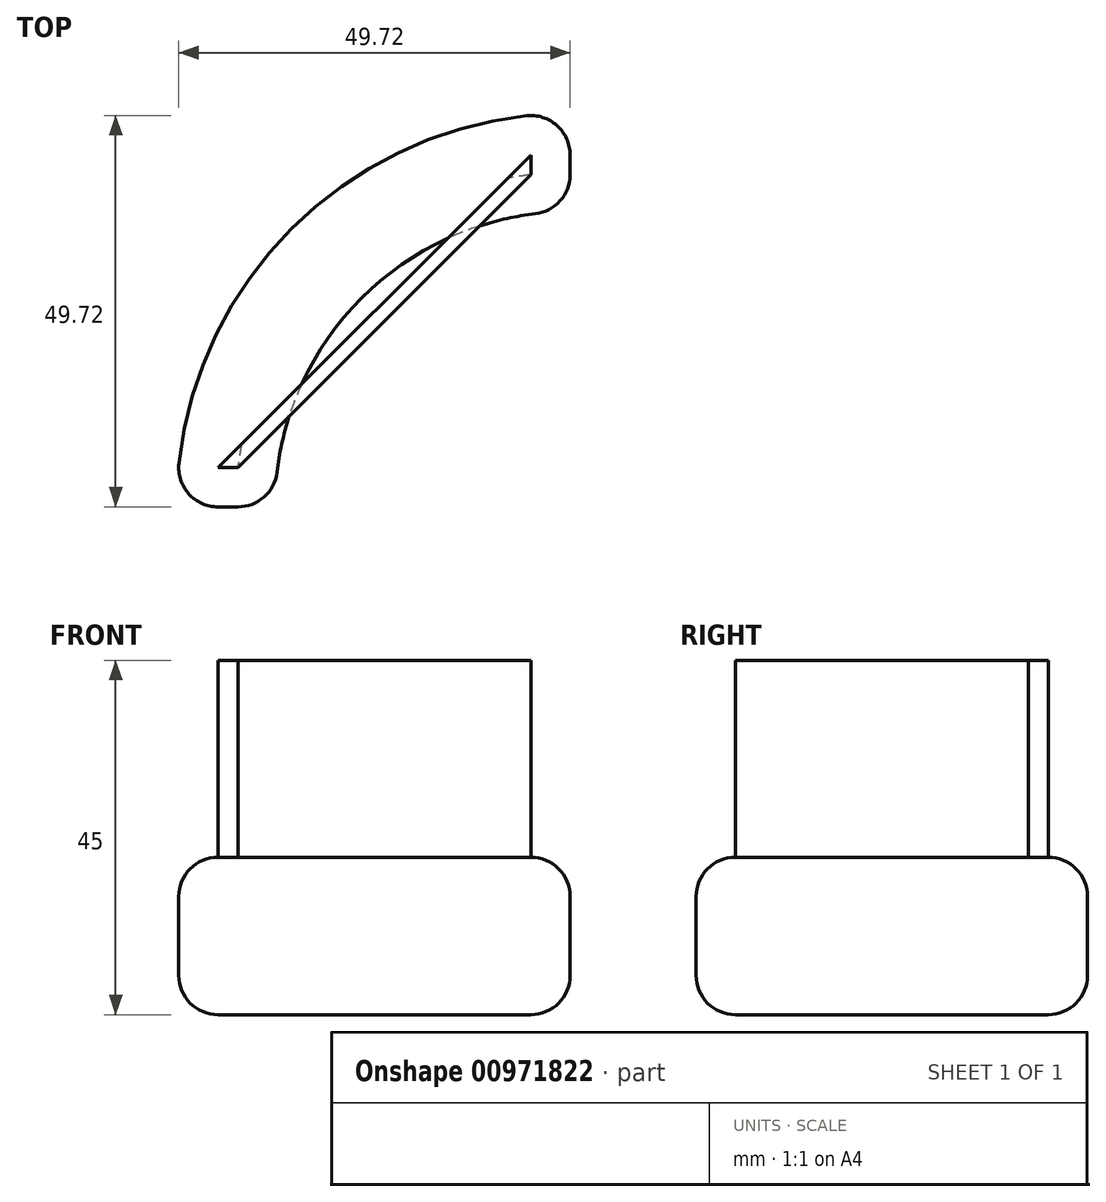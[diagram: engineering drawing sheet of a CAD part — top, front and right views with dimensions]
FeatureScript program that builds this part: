
annotation { "Feature Type Name" : "Feature", "Feature Type Description" : "" }
export const myFeature = defineFeature(function(context is Context, id is Id, definition is map)
    precondition{}
    {
        {
            var Q0;
            Q0=qCreatedBy(makeId("Top.planeOp"),FACE);
            var sketch = newSketch(context, id + "F0", { "sketchPlane" : qUnion([Q0])});
            skArc(sketch, "E0", {"start": v(0, 50) * mm, "mid": v(-35.36, 35.36) * mm, "end": v(-50, 0) * mm});
            skArc(sketch, "E1", {"start": v(0, 37.5) * mm, "mid": v(-26.52, 26.52) * mm, "end": v(-37.5, 0) * mm});
            skLineSegment(sketch, "E2", {"start": v(0, 37.5) * mm, "end": v(0, 50) * mm});
            skLineSegment(sketch, "E3", {"start": v(-37.5, 0) * mm, "end": v(-50, 0) * mm});
            skPoint(sketch, "E4", {"position": v(-37.5, 0) * mm});
            skPoint(sketch, "E5", {"position": v(0, 37.5) * mm});
            skSolve(sketch);
        }
        {
            var Q0;
            Q0 = qSketchRegion(id + "F0", true);
            extrude(context, id + "F1", {"entities" : qUnion([Q0]), "depth" : 20 * mm, "offsetDistance" : 25 * mm});
        }
        {
            var Q0;
            Q0=makeQuery(id+"F1.opExtrude","CAP_EDGE",EDGE,{"disambiguationData":[OSD([sQuery(id+"F0.wireOp",EDGE,"E1")])],"isStart":true});
            var Q1;
            Q1=makeQuery(id+"F1.opExtrude","CAP_EDGE",EDGE,{"disambiguationData":[OSD([sQuery(id+"F0.wireOp",EDGE,"E1")])],"isStart":false});
            var Q2;
            Q2=makeQuery(id+"F1.opExtrude","CAP_EDGE",EDGE,{"disambiguationData":[OSD([sQuery(id+"F0.wireOp",EDGE,"E3")])],"isStart":true});
            var Q3;
            Q3=makeQuery(id+"F1.opExtrude","CAP_EDGE",EDGE,{"disambiguationData":[OSD([sQuery(id+"F0.wireOp",EDGE,"E3")])],"isStart":false});
            var Q4;
            Q4=makeQuery(id+"F1.opExtrude","CAP_EDGE",EDGE,{"disambiguationData":[OSD([sQuery(id+"F0.wireOp",EDGE,"E2")])],"isStart":true});
            var Q5;
            Q5=makeQuery(id+"F1.opExtrude","CAP_EDGE",EDGE,{"disambiguationData":[OSD([sQuery(id+"F0.wireOp",EDGE,"E2")])],"isStart":false});
            var Q6;
            Q6=makeQuery(id+"F1.opExtrude","SWEPT_EDGE",EDGE,{"disambiguationData":[OSD([sQuery(id+"F0.wireOp",EDGE,"E0"),sQuery(id+"F0.wireOp",EDGE,"E3")])]});
            var Q7;
            Q7=makeQuery(id+"F1.opExtrude","SWEPT_EDGE",EDGE,{"disambiguationData":[OSD([sQuery(id+"F0.wireOp",EDGE,"E0"),sQuery(id+"F0.wireOp",EDGE,"E2")])]});
            var Q8;
            Q8=makeQuery(id+"F1.opExtrude","SWEPT_EDGE",EDGE,{"disambiguationData":[OSD([sQuery(id+"F0.wireOp",EDGE,"E1"),sQuery(id+"F0.wireOp",EDGE,"E2")])]});
            var Q9;
            Q9=makeQuery(id+"F1.opExtrude","SWEPT_EDGE",EDGE,{"disambiguationData":[OSD([sQuery(id+"F0.wireOp",EDGE,"E1"),sQuery(id+"F0.wireOp",EDGE,"E3")])]});
            var Q10;
            Q10=makeQuery(id+"F1.opExtrude","CAP_EDGE",EDGE,{"disambiguationData":[OSD([sQuery(id+"F0.wireOp",EDGE,"E0")])],"isStart":true});
            var Q11;
            Q11=makeQuery(id+"F1.opExtrude","CAP_EDGE",EDGE,{"disambiguationData":[OSD([sQuery(id+"F0.wireOp",EDGE,"E0")])],"isStart":false});
            fillet(context, id + "F2", {"entities" : qUnion([Q0, Q1, Q2, Q3, Q4, Q5, Q6, Q7, Q8, Q9, Q10, Q11]), "radius" : 5 * mm, "tangentPropagation" : true, "allowEdgeOverflow" : false});
        }
        {
            var Q0;
            Q0=makeQuery(id+"F1.opExtrude","CAP_FACE",FACE,{"disambiguationData":[OSD([sQuery(id+"F0.wireOp",EDGE,"E0"),sQuery(id+"F0.wireOp",EDGE,"E1"),sQuery(id+"F0.wireOp",EDGE,"E2"),sQuery(id+"F0.wireOp",EDGE,"E3")])],"isStart":false});
            var sketch = newSketch(context, id + "F3", { "sketchPlane" : qUnion([Q0])});
            skLineSegment(sketch, "E6", {"start": v(-44.72, 5) * mm, "end": v(-42.2, 5) * mm});
            skLineSegment(sketch, "E7", {"start": v(-42.2, 5) * mm, "end": v(-5, 42.2) * mm});
            skLineSegment(sketch, "E8", {"start": v(-5, 42.2) * mm, "end": v(-5, 44.72) * mm});
            skLineSegment(sketch, "E9", {"start": v(-5, 44.72) * mm, "end": v(-44.72, 5) * mm});
            skSolve(sketch);
        }
        {
            var Q0;
            Q0 = qSketchRegion(id + "F3", true);
            extrude(context, id + "F4", {"entities" : qUnion([Q0]), "operationType" : NewBodyOperationType.ADD, "depth" : 25 * mm, "offsetDistance" : 25 * mm});
        }
    });
